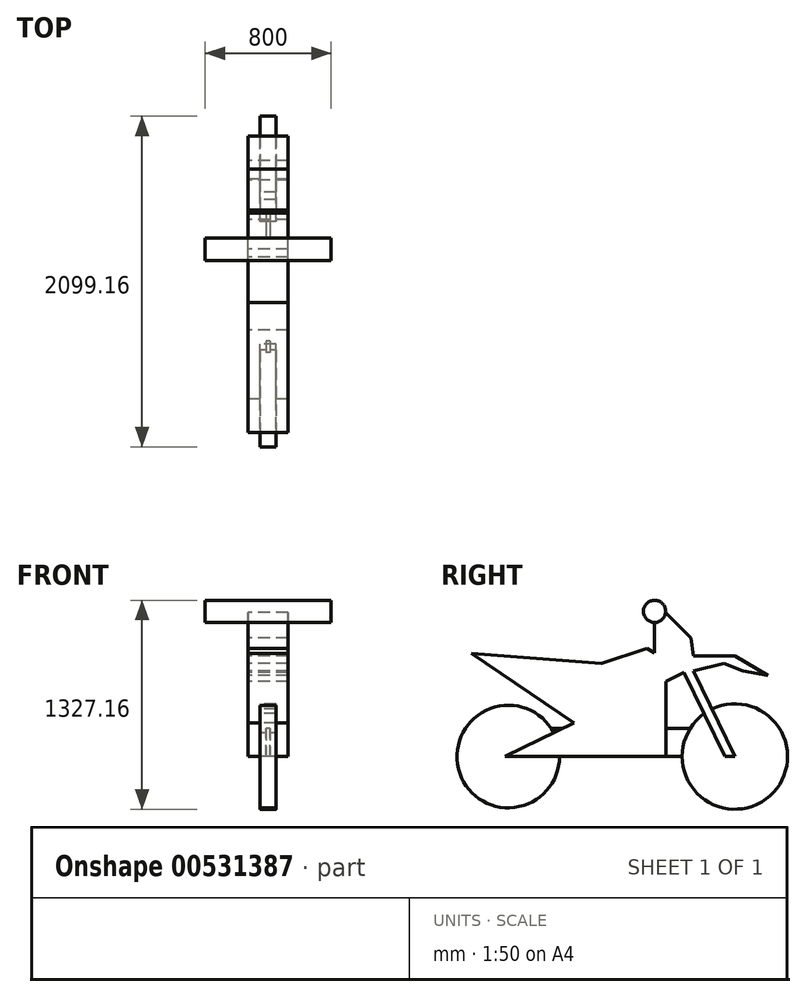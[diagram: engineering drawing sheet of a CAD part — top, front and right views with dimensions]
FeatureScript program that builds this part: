
annotation { "Feature Type Name" : "Feature", "Feature Type Description" : "" }
export const myFeature = defineFeature(function(context is Context, id is Id, definition is map)
    precondition{}
    {
        {
            var Q0;
            Q0=qCreatedBy(makeId("Right.planeOp"),FACE);
            var sketch = newSketch(context, id + "F0", { "sketchPlane" : qUnion([Q0])});
            skCircle(sketch, "E0", {"center": v(-1447.8, 0) * mm, "radius": 228.6 * mm});
            skCircle(sketch, "E1", {"center": v(0, 0) * mm, "radius": 266.7 * mm});
            skSolve(sketch);
        }
        {
            var Q0;
            Q0=makeQuery(id+"F0.imprint","IMPRINT",FACE,{"disambiguationData":[TD([[makeQuery(id+"F0.imprint","IMPRINT",EDGE,{"derivedFrom":sQuery(id+"F0.wireOp",EDGE,"E1")}),1.0]])]});
            extrude(context, id + "F1", {"entities" : qUnion([Q0]), "endBound" : BoundingType.SYMMETRIC, "depth" : 76.2 * mm, "offsetDistance" : 25.4 * mm});
        }
        {
            var Q0;
            Q0=makeQuery(id+"F0.imprint","IMPRINT",FACE,{"disambiguationData":[TD([[makeQuery(id+"F0.imprint","IMPRINT",EDGE,{"derivedFrom":sQuery(id+"F0.wireOp",EDGE,"E0")}),1.0]])]});
            extrude(context, id + "F2", {"entities" : qUnion([Q0]), "operationType" : NewBodyOperationType.ADD, "endBound" : BoundingType.SYMMETRIC, "depth" : 101.6 * mm, "offsetDistance" : 25.4 * mm});
        }
        {
            var Q0;
            Q0=qCreatedBy(makeId("Right.planeOp"),FACE);
            var sketch = newSketch(context, id + "F3", { "sketchPlane" : qUnion([Q0])});
            skLineSegment(sketch, "E2.bottom", {"start": v(0, 0) * mm, "end": v(-1447.8, 0) * mm});
            skLineSegment(sketch, "E2.top", {"start": v(0, 177.8) * mm, "end": v(-1447.8, 177.8) * mm});
            skLineSegment(sketch, "E2.left", {"start": v(0, 0) * mm, "end": v(0, 177.8) * mm});
            skLineSegment(sketch, "E2.right", {"start": v(-1447.8, 0) * mm, "end": v(-1447.8, 177.8) * mm});
            skSolve(sketch);
        }
        {
            var Q0;
            Q0=makeQuery(id+"F3.imprint","IMPRINT",FACE,{"disambiguationData":[TD([[makeQuery(id+"F3.imprint","IMPRINT",EDGE,{"derivedFrom":sQuery(id+"F3.wireOp",EDGE,"E2.bottom")}),-1.0]])]});
            extrude(context, id + "F4", {"entities" : qUnion([Q0]), "operationType" : NewBodyOperationType.ADD, "endBound" : BoundingType.SYMMETRIC, "depth" : 25.4 * mm, "offsetDistance" : 25.4 * mm});
        }
        {
            var Q0;
            Q0=qCreatedBy(makeId("Right.planeOp"),FACE);
            var sketch = newSketch(context, id + "F5", { "sketchPlane" : qUnion([Q0])});
            skLineSegment(sketch, "E3", {"start": v(-1672.22, 654.36) * mm, "end": v(-848.04, 592.4) * mm});
            skLineSegment(sketch, "E4", {"start": v(-848.04, 592.4) * mm, "end": v(-558.85, 685.35) * mm});
            skLineSegment(sketch, "E5", {"start": v(-558.85, 685.35) * mm, "end": v(-509.28, 656.43) * mm});
            skLineSegment(sketch, "E6", {"start": v(-509.28, 656.43) * mm, "end": v(-509.28, 922.9) * mm});
            skLineSegment(sketch, "E7", {"start": v(-509.28, 922.9) * mm, "end": v(-447.3, 922.9) * mm});
            skLineSegment(sketch, "E8", {"start": v(-447.3, 922.9) * mm, "end": v(-280, 753.51) * mm});
            skLineSegment(sketch, "E9", {"start": v(-280, 753.51) * mm, "end": v(-261.4, 637.84) * mm});
            skLineSegment(sketch, "E10", {"start": v(-261.4, 637.84) * mm, "end": v(0, 637.84) * mm});
            skLineSegment(sketch, "E11", {"start": v(0, 637.84) * mm, "end": v(209.56, 515.97) * mm});
            skLineSegment(sketch, "E12", {"start": v(209.56, 515.97) * mm, "end": v(52.57, 544.89) * mm});
            skLineSegment(sketch, "E13", {"start": v(52.57, 544.89) * mm, "end": v(-69.3, 590.33) * mm});
            skLineSegment(sketch, "E14", {"start": v(-69.3, 590.33) * mm, "end": v(-263.47, 544.89) * mm});
            skLineSegment(sketch, "E15", {"start": v(-263.47, 544.89) * mm, "end": v(0, 0) * mm});
            skLineSegment(sketch, "E16", {"start": v(0, 0) * mm, "end": v(-63.1, 0) * mm});
            skLineSegment(sketch, "E17", {"start": v(-63.1, 0) * mm, "end": v(-321.84, 535.1) * mm});
            skLineSegment(sketch, "E18", {"start": v(-321.84, 535.1) * mm, "end": v(-438.96, 478.46) * mm});
            skLineSegment(sketch, "E19", {"start": v(-438.96, 478.46) * mm, "end": v(-438.96, 0) * mm});
            skLineSegment(sketch, "E20", {"start": v(-438.96, 0) * mm, "end": v(-1219.85, 0) * mm});
            skLineSegment(sketch, "E21", {"start": v(-1219.85, 0) * mm, "end": v(-1459.46, 0) * mm});
            skLineSegment(sketch, "E22", {"start": v(-1459.46, 0) * mm, "end": v(-1021.32, 211.85) * mm});
            skLineSegment(sketch, "E23", {"start": v(-1021.32, 211.85) * mm, "end": v(-1672.22, 654.36) * mm});
            skSolve(sketch);
        }
        {
            var Q0;
            Q0=makeQuery(id+"F5.imprint","IMPRINT",FACE,{"disambiguationData":[TD([[makeQuery(id+"F5.imprint","IMPRINT",EDGE,{"derivedFrom":sQuery(id+"F5.wireOp",EDGE,"E3")}),-1.0]])]});
            extrude(context, id + "F6", {"entities" : qUnion([Q0]), "operationType" : NewBodyOperationType.ADD, "endBound" : BoundingType.SYMMETRIC, "depth" : 254 * mm, "offsetDistance" : 25.4 * mm});
        }
        {
            var Q0;
            Q0=qCreatedBy(makeId("Right.planeOp"),FACE);
            var sketch = newSketch(context, id + "F7", { "sketchPlane" : qUnion([Q0])});
            skCircle(sketch, "E24", {"center": v(0, 0) * mm, "radius": 334.77 * mm});
            skCircle(sketch, "E25", {"center": v(-1438.7, 0) * mm, "radius": 325.69 * mm});
            skSolve(sketch);
        }
        {
            var Q0;
            Q0=makeQuery(id+"F7.imprint","IMPRINT",FACE,{"disambiguationData":[TD([[makeQuery(id+"F7.imprint","IMPRINT",EDGE,{"derivedFrom":sQuery(id+"F7.wireOp",EDGE,"E25")}),1.0]])]});
            var Q1;
            Q1=makeQuery(id+"F7.imprint","IMPRINT",FACE,{"disambiguationData":[TD([[makeQuery(id+"F7.imprint","IMPRINT",EDGE,{"derivedFrom":sQuery(id+"F7.wireOp",EDGE,"E24")}),1.0]])]});
            extrude(context, id + "F8", {"entities" : qUnion([Q0, Q1]), "operationType" : NewBodyOperationType.ADD, "endBound" : BoundingType.SYMMETRIC, "depth" : 101.6 * mm, "offsetDistance" : 25.4 * mm});
        }
        {
            var Q0;
            Q0=qCreatedBy(makeId("Right.planeOp"),FACE);
            var sketch = newSketch(context, id + "F9", { "sketchPlane" : qUnion([Q0])});
            skCircle(sketch, "E26", {"center": v(-509.71, 921.78) * mm, "radius": 70.6 * mm});
            skSolve(sketch);
        }
        {
            var Q0;
            Q0=makeQuery(id+"F9.imprint","IMPRINT",FACE,{"disambiguationData":[TD([[makeQuery(id+"F9.imprint","IMPRINT",EDGE,{"derivedFrom":sQuery(id+"F9.wireOp",EDGE,"E26")}),1.0]])]});
            var Q1;
            Q1=sQuery(id+"F9.wireOp",EDGE,"E26");
            extrude(context, id + "F10", {"entities" : qUnion([Q0]), "operationType" : NewBodyOperationType.ADD, "surfaceEntities" : qUnion([Q1]), "endBound" : BoundingType.SYMMETRIC, "depth" : 800 * mm, "offsetDistance" : 25.4 * mm});
        }
    });
